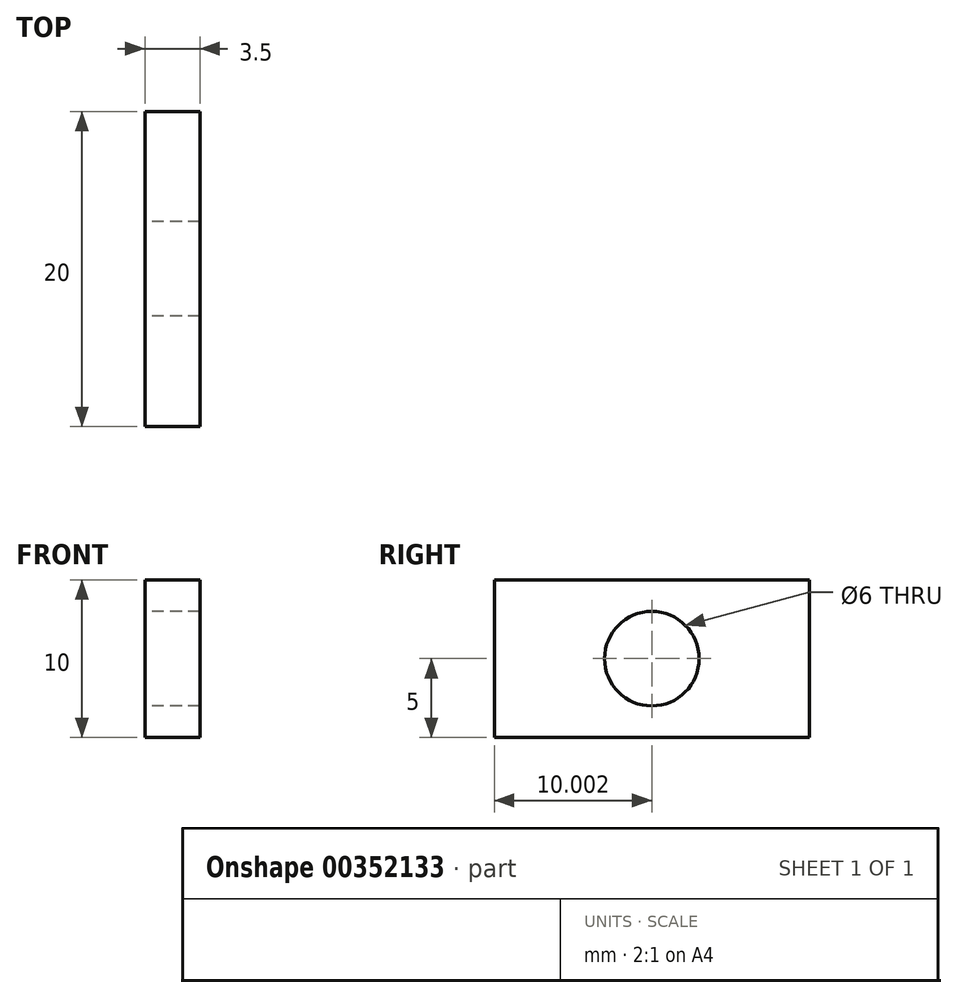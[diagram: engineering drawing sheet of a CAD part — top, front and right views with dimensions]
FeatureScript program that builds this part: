
annotation { "Feature Type Name" : "Feature", "Feature Type Description" : "" }
export const myFeature = defineFeature(function(context is Context, id is Id, definition is map)
    precondition{}
    {
        {
            var Q0;
            Q0=qCreatedBy(makeId("Top.planeOp"),FACE);
            var sketch = newSketch(context, id + "F0", { "sketchPlane" : qUnion([Q0])});
            skLineSegment(sketch, "E0.bottom", {"start": v(0, 0.57) * mm, "end": v(3.5, 0.57) * mm});
            skLineSegment(sketch, "E0.top", {"start": v(0, 20.57) * mm, "end": v(3.5, 20.57) * mm});
            skLineSegment(sketch, "E0.left", {"start": v(0, 0.57) * mm, "end": v(0, 20.57) * mm});
            skLineSegment(sketch, "E0.right", {"start": v(3.5, 0.57) * mm, "end": v(3.5, 20.57) * mm});
            skSolve(sketch);
        }
        {
            var Q0;
            Q0=makeQuery(id+"F0.imprint","IMPRINT",FACE,{"disambiguationData":[TD([[makeQuery(id+"F0.imprint","IMPRINT",EDGE,{"derivedFrom":sQuery(id+"F0.wireOp",EDGE,"E0.bottom")}),1.0]])]});
            extrude(context, id + "F1", {"entities" : qUnion([Q0]), "depth" : 10 * mm});
        }
        {
            var Q0;
            Q0=makeQuery(id+"F1.opExtrude","SWEPT_FACE",FACE,{"disambiguationData":[OSD([sQuery(id+"F0.wireOp",EDGE,"E0.left")])]});
            var sketch = newSketch(context, id + "F2", { "sketchPlane" : qUnion([Q0])});
            skLineSegment(sketch, "E1", {"start": v(-20.57, 10) * mm, "end": v(-0.57, 0) * mm, "construction": true});
            skLineSegment(sketch, "E2", {"start": v(-0.57, 10) * mm, "end": v(-20.57, 0) * mm, "construction": true});
            skPoint(sketch, "E3", {"position": v(-10.57, 5) * mm});
            skSolve(sketch);
        }
        {
            var Q0;
            Q0=sQuery(id+"F2.wireOp",VERTEX,"E3");
            var Q1;
            Q1=makeQuery(id+"F1.opExtrude","SWEPT_BODY",BODY,{"disambiguationData":[OSD([sQuery(id+"F0.wireOp",EDGE,"E0.bottom"),sQuery(id+"F0.wireOp",EDGE,"E0.top"),sQuery(id+"F0.wireOp",EDGE,"E0.left"),sQuery(id+"F0.wireOp",EDGE,"E0.right")])]});
            hole(context, id + "F3", {"style" : HoleStyle.SIMPLE, "endStyle" : HoleEndStyle.THROUGH, "holeDiameter" : 6 * mm, "isTappedThrough" : true, "tappedDepth" : 12 * mm, "tapClearance" : 3, "locations" : qUnion([Q0]), "scope" : qUnion([Q1])});
        }
    });
